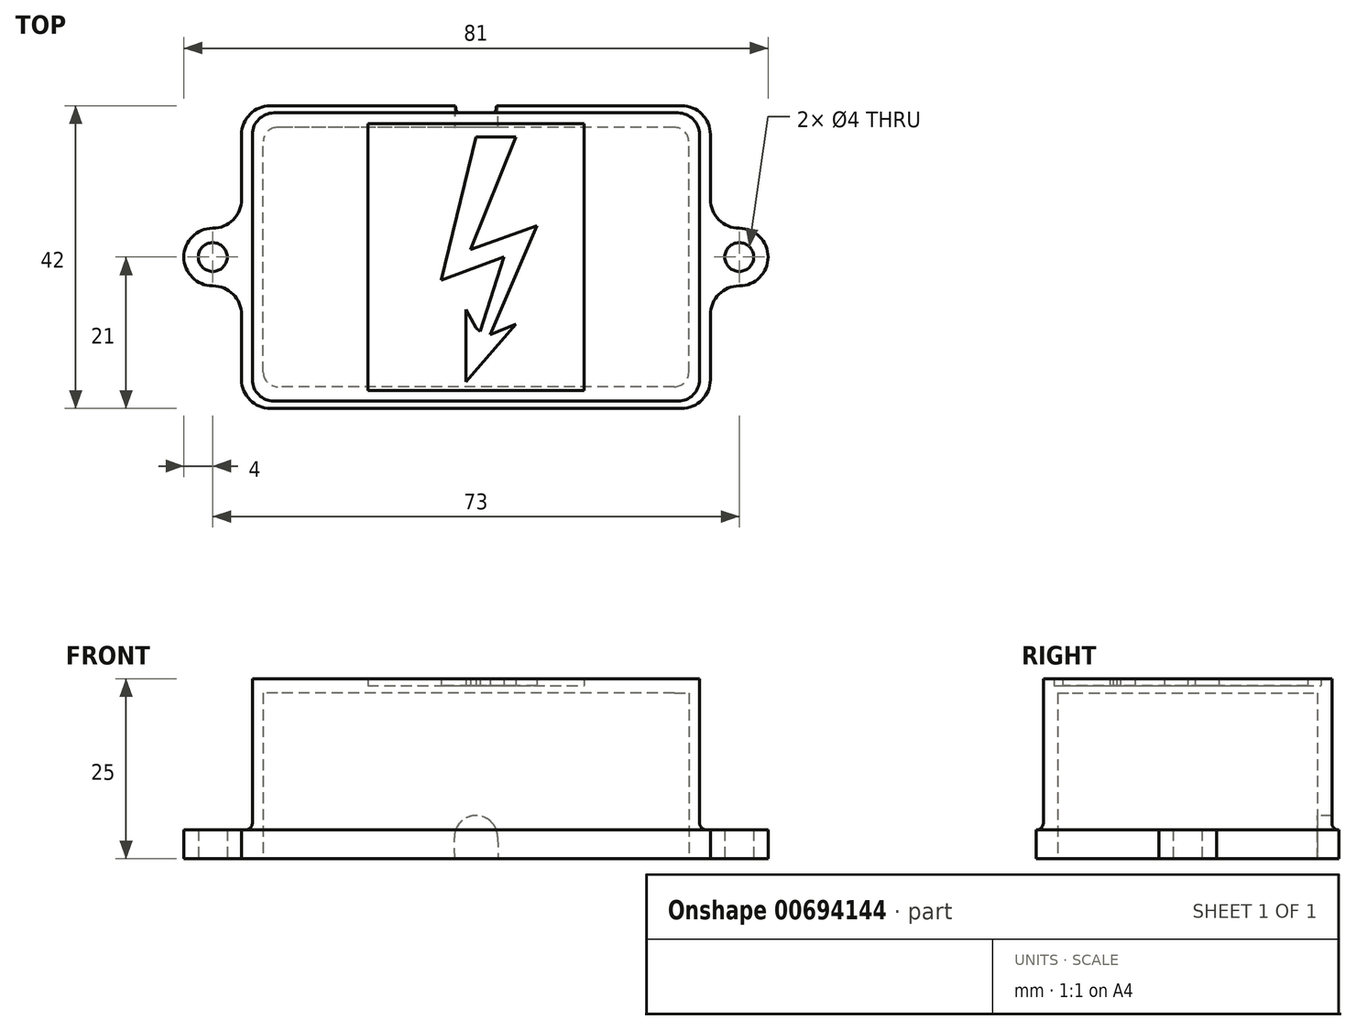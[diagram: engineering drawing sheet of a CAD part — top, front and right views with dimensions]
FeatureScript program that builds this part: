
annotation { "Feature Type Name" : "Feature", "Feature Type Description" : "" }
export const myFeature = defineFeature(function(context is Context, id is Id, definition is map)
    precondition{}
    {
        {
            var Q0;
            Q0=qCreatedBy(makeId("Top.planeOp"),FACE);
            var sketch = newSketch(context, id + "F0", { "sketchPlane" : qUnion([Q0])});
            skLineSegment(sketch, "E0.bottom", {"start": v(-28.5, 21) * mm, "end": v(28.5, 21) * mm});
            skLineSegment(sketch, "E0.top", {"start": v(-28.5, -21) * mm, "end": v(28.5, -21) * mm});
            skLineSegment(sketch, "E0.left", {"start": v(-32.5, 17) * mm, "end": v(-32.5, 8) * mm});
            skLineSegment(sketch, "E0.right", {"start": v(32.5, 17) * mm, "end": v(32.5, 8) * mm});
            skPoint(sketch, "E0.middle", {"position": v(0, 0) * mm});
            skPoint(sketch, "E1.visualSharp", {"position": v(-32.5, 21) * mm});
            skArc(sketch, "E1.filletArc", {"start": v(-28.5, 21) * mm, "mid": v(-31.33, 19.83) * mm, "end": v(-32.5, 17) * mm});
            skPoint(sketch, "E2.visualSharp", {"position": v(-32.5, -21) * mm});
            skArc(sketch, "E2.filletArc", {"start": v(-32.5, -17) * mm, "mid": v(-31.33, -19.83) * mm, "end": v(-28.5, -21) * mm});
            skPoint(sketch, "E3.visualSharp", {"position": v(32.5, -21) * mm});
            skArc(sketch, "E3.filletArc", {"start": v(28.5, -21) * mm, "mid": v(31.33, -19.83) * mm, "end": v(32.5, -17) * mm});
            skPoint(sketch, "E4.visualSharp", {"position": v(32.5, 21) * mm});
            skArc(sketch, "E4.filletArc", {"start": v(32.5, 17) * mm, "mid": v(31.33, 19.83) * mm, "end": v(28.5, 21) * mm});
            skLineSegment(sketch, "E5", {"start": v(0, 0) * mm, "end": v(36.5, 0) * mm, "construction": true});
            skCircle(sketch, "E6", {"center": v(36.5, 0) * mm, "radius": 2 * mm});
            skArc(sketch, "E7", {"start": v(36.5, -4) * mm, "mid": v(40.5, 0) * mm, "end": v(36.5, 4) * mm});
            skLineSegment(sketch, "E8", {"start": v(36.5, -4) * mm, "end": v(36.5, -4) * mm});
            skLineSegment(sketch, "E9.MirrorCS", {"start": v(36.5, 4) * mm, "end": v(36.5, 4) * mm});
            skLineSegment(sketch, "E10.MirrorCS", {"start": v(-36.5, 4) * mm, "end": v(-36.5, 4) * mm});
            skArc(sketch, "E11.MirrorC", {"start": v(-36.5, -4) * mm, "mid": v(-40.5, 0) * mm, "end": v(-36.5, 4) * mm});
            skLineSegment(sketch, "E12.MirrorCS", {"start": v(-36.5, -4) * mm, "end": v(-36.5, -4) * mm});
            skCircle(sketch, "E13.MirrorC", {"center": v(-36.5, 0) * mm, "radius": 2 * mm});
            skLineSegment(sketch, "E14.trimOffspring", {"start": v(-32.5, -8) * mm, "end": v(-32.5, -17) * mm});
            skLineSegment(sketch, "E15.trimOffspring", {"start": v(32.5, -8) * mm, "end": v(32.5, -17) * mm});
            skPoint(sketch, "E16.visualSharp", {"position": v(-32.5, 4) * mm});
            skArc(sketch, "E16.filletArc", {"start": v(-36.5, 4) * mm, "mid": v(-33.67, 5.17) * mm, "end": v(-32.5, 8) * mm});
            skPoint(sketch, "E17.visualSharp", {"position": v(-32.5, -4) * mm});
            skArc(sketch, "E17.filletArc", {"start": v(-32.5, -8) * mm, "mid": v(-33.67, -5.17) * mm, "end": v(-36.5, -4) * mm});
            skPoint(sketch, "E18.visualSharp", {"position": v(32.5, -4) * mm});
            skArc(sketch, "E18.filletArc", {"start": v(36.5, -4) * mm, "mid": v(33.67, -5.17) * mm, "end": v(32.5, -8) * mm});
            skPoint(sketch, "E19.visualSharp", {"position": v(32.5, 4) * mm});
            skArc(sketch, "E19.filletArc", {"start": v(32.5, 8) * mm, "mid": v(33.67, 5.17) * mm, "end": v(36.5, 4) * mm});
            skLineSegment(sketch, "E20.bottom", {"start": v(27.5, -18) * mm, "end": v(-27.5, -18) * mm});
            skLineSegment(sketch, "E20.top", {"start": v(27.5, 18) * mm, "end": v(-27.5, 18) * mm});
            skLineSegment(sketch, "E20.left", {"start": v(29.5, -16) * mm, "end": v(29.5, 16) * mm});
            skLineSegment(sketch, "E20.right", {"start": v(-29.5, -16) * mm, "end": v(-29.5, 16) * mm});
            skPoint(sketch, "E21.visualSharp", {"position": v(-29.5, -18) * mm});
            skArc(sketch, "E21.filletArc", {"start": v(-29.5, -16) * mm, "mid": v(-28.91, -17.41) * mm, "end": v(-27.5, -18) * mm});
            skPoint(sketch, "E22.visualSharp", {"position": v(29.5, 18) * mm});
            skArc(sketch, "E22.filletArc", {"start": v(29.5, 16) * mm, "mid": v(28.91, 17.41) * mm, "end": v(27.5, 18) * mm});
            skPoint(sketch, "E23.visualSharp", {"position": v(29.5, -18) * mm});
            skArc(sketch, "E23.filletArc", {"start": v(27.5, -18) * mm, "mid": v(28.91, -17.41) * mm, "end": v(29.5, -16) * mm});
            skPoint(sketch, "E24.visualSharp", {"position": v(-29.5, 18) * mm});
            skArc(sketch, "E24.filletArc", {"start": v(-27.5, 18) * mm, "mid": v(-28.91, 17.41) * mm, "end": v(-29.5, 16) * mm});
            skSolve(sketch);
        }
        {
            var Q0;
            Q0=makeQuery(id+"F0.imprint","IMPRINT",FACE,{"disambiguationData":[TD([[makeQuery(id+"F0.imprint","IMPRINT",EDGE,{"derivedFrom":sQuery(id+"F0.wireOp",EDGE,"E0.bottom")}),-1.0]])]});
            extrude(context, id + "F1", {"entities" : qUnion([Q0]), "depth" : 4 * mm, "offsetDistance" : 25 * mm});
        }
        {
            var Q0;
            Q0=qCreatedBy(makeId("Top.planeOp"),FACE);
            var sketch = newSketch(context, id + "F2", { "sketchPlane" : qUnion([Q0])});
            skLineSegment(sketch, "E25.bottom", {"start": v(-28, 20) * mm, "end": v(28, 20) * mm});
            skLineSegment(sketch, "E25.top", {"start": v(-28, -20) * mm, "end": v(28, -20) * mm});
            skLineSegment(sketch, "E25.left", {"start": v(-31, 17) * mm, "end": v(-31, -17) * mm});
            skLineSegment(sketch, "E25.right", {"start": v(31, 17) * mm, "end": v(31, -17) * mm});
            skPoint(sketch, "E25.middle", {"position": v(0, 0) * mm});
            skPoint(sketch, "E26.visualSharp", {"position": v(-31, 20) * mm});
            skArc(sketch, "E26.filletArc", {"start": v(-28, 20) * mm, "mid": v(-30.12, 19.12) * mm, "end": v(-31, 17) * mm});
            skPoint(sketch, "E27.visualSharp", {"position": v(31, 20) * mm});
            skArc(sketch, "E27.filletArc", {"start": v(31, 17) * mm, "mid": v(30.12, 19.12) * mm, "end": v(28, 20) * mm});
            skPoint(sketch, "E28.visualSharp", {"position": v(31, -20) * mm});
            skArc(sketch, "E28.filletArc", {"start": v(28, -20) * mm, "mid": v(30.12, -19.12) * mm, "end": v(31, -17) * mm});
            skPoint(sketch, "E29.visualSharp", {"position": v(-31, -20) * mm});
            skArc(sketch, "E29.filletArc", {"start": v(-31, -17) * mm, "mid": v(-30.12, -19.12) * mm, "end": v(-28, -20) * mm});
            skSolve(sketch);
        }
        {
            var Q0;
            Q0 = qSketchRegion(id + "F2", true);
            extrude(context, id + "F3", {"entities" : qUnion([Q0]), "operationType" : NewBodyOperationType.ADD, "depth" : 25 * mm, "offsetDistance" : 25 * mm});
        }
        {
            var Q0;
            Q0=makeQuery(id+"F3.boolean.opBoolean","INTERSECT",EDGE,{"derivedFrom":[makeQuery(id+"F1.opExtrude","CAP_FACE",FACE,{"disambiguationData":[OSD([sQuery(id+"F0.wireOp",EDGE,"E0.bottom"),sQuery(id+"F0.wireOp",EDGE,"E0.top"),sQuery(id+"F0.wireOp",EDGE,"E0.left"),sQuery(id+"F0.wireOp",EDGE,"E0.right"),sQuery(id+"F0.wireOp",EDGE,"E1.filletArc"),sQuery(id+"F0.wireOp",EDGE,"E2.filletArc"),sQuery(id+"F0.wireOp",EDGE,"E3.filletArc"),sQuery(id+"F0.wireOp",EDGE,"E4.filletArc"),sQuery(id+"F0.wireOp",EDGE,"E6"),sQuery(id+"F0.wireOp",EDGE,"E7"),sQuery(id+"F0.wireOp",EDGE,"E11.MirrorC"),sQuery(id+"F0.wireOp",EDGE,"E13.MirrorC"),sQuery(id+"F0.wireOp",EDGE,"E14.trimOffspring"),sQuery(id+"F0.wireOp",EDGE,"E15.trimOffspring"),sQuery(id+"F0.wireOp",EDGE,"E16.filletArc"),sQuery(id+"F0.wireOp",EDGE,"E17.filletArc"),sQuery(id+"F0.wireOp",EDGE,"E18.filletArc"),sQuery(id+"F0.wireOp",EDGE,"E19.filletArc"),sQuery(id+"F0.wireOp",EDGE,"E20.bottom"),sQuery(id+"F0.wireOp",EDGE,"E20.top"),sQuery(id+"F0.wireOp",EDGE,"E20.left"),sQuery(id+"F0.wireOp",EDGE,"E20.right"),sQuery(id+"F0.wireOp",EDGE,"E21.filletArc"),sQuery(id+"F0.wireOp",EDGE,"E22.filletArc"),sQuery(id+"F0.wireOp",EDGE,"E23.filletArc"),sQuery(id+"F0.wireOp",EDGE,"E24.filletArc")])],"isStart":false}),makeQuery(id+"F3.opExtrude","SWEPT_FACE",FACE,{"disambiguationData":[OSD([sQuery(id+"F2.wireOp",EDGE,"E25.top")])]})]});
            var Q1;
            Q1=makeQuery(id+"F3.boolean.opBoolean","INTERSECT",EDGE,{"derivedFrom":[makeQuery(id+"F1.opExtrude","CAP_FACE",FACE,{"disambiguationData":[OSD([sQuery(id+"F0.wireOp",EDGE,"E0.bottom"),sQuery(id+"F0.wireOp",EDGE,"E0.top"),sQuery(id+"F0.wireOp",EDGE,"E0.left"),sQuery(id+"F0.wireOp",EDGE,"E0.right"),sQuery(id+"F0.wireOp",EDGE,"E1.filletArc"),sQuery(id+"F0.wireOp",EDGE,"E2.filletArc"),sQuery(id+"F0.wireOp",EDGE,"E3.filletArc"),sQuery(id+"F0.wireOp",EDGE,"E4.filletArc"),sQuery(id+"F0.wireOp",EDGE,"E6"),sQuery(id+"F0.wireOp",EDGE,"E7"),sQuery(id+"F0.wireOp",EDGE,"E11.MirrorC"),sQuery(id+"F0.wireOp",EDGE,"E13.MirrorC"),sQuery(id+"F0.wireOp",EDGE,"E14.trimOffspring"),sQuery(id+"F0.wireOp",EDGE,"E15.trimOffspring"),sQuery(id+"F0.wireOp",EDGE,"E16.filletArc"),sQuery(id+"F0.wireOp",EDGE,"E17.filletArc"),sQuery(id+"F0.wireOp",EDGE,"E18.filletArc"),sQuery(id+"F0.wireOp",EDGE,"E19.filletArc"),sQuery(id+"F0.wireOp",EDGE,"E20.bottom"),sQuery(id+"F0.wireOp",EDGE,"E20.top"),sQuery(id+"F0.wireOp",EDGE,"E20.left"),sQuery(id+"F0.wireOp",EDGE,"E20.right"),sQuery(id+"F0.wireOp",EDGE,"E21.filletArc"),sQuery(id+"F0.wireOp",EDGE,"E22.filletArc"),sQuery(id+"F0.wireOp",EDGE,"E23.filletArc"),sQuery(id+"F0.wireOp",EDGE,"E24.filletArc")])],"isStart":false}),makeQuery(id+"F3.opExtrude","SWEPT_FACE",FACE,{"disambiguationData":[OSD([sQuery(id+"F2.wireOp",EDGE,"E28.filletArc")])]})]});
            fillet(context, id + "F4", {"entities" : qUnion([Q0, Q1]), "radius" : 1 * mm, "tangentPropagation" : true, "allowEdgeOverflow" : false});
        }
        {
            var Q0;
            Q0=makeQuery(id+"F0.imprint","IMPRINT",FACE,{"disambiguationData":[TD([[makeQuery(id+"F0.imprint","IMPRINT",EDGE,{"derivedFrom":sQuery(id+"F0.wireOp",EDGE,"E20.bottom")}),-1.0]])]});
            extrude(context, id + "F5", {"entities" : qUnion([Q0]), "operationType" : NewBodyOperationType.REMOVE, "depth" : 23 * mm, "offsetDistance" : 25 * mm});
        }
        {
            var Q0;
            Q0=qCreatedBy(makeId("Top.planeOp"),FACE);
            var sketch = newSketch(context, id + "F6", { "sketchPlane" : qUnion([Q0])});
            skLineSegment(sketch, "E30", {"start": v(0, 16.64) * mm, "end": v(5.54, 16.64) * mm});
            skLineSegment(sketch, "E31", {"start": v(5.54, 16.64) * mm, "end": v(-0.76, 1.03) * mm});
            skLineSegment(sketch, "E32", {"start": v(-0.76, 1.03) * mm, "end": v(8.45, 4.35) * mm});
            skLineSegment(sketch, "E33", {"start": v(8.45, 4.35) * mm, "end": v(1.98, -10.77) * mm});
            skLineSegment(sketch, "E34", {"start": v(1.98, -10.77) * mm, "end": v(5.54, -9.32) * mm});
            skLineSegment(sketch, "E35", {"start": v(5.54, -9.32) * mm, "end": v(-1.41, -17.32) * mm});
            skLineSegment(sketch, "E36", {"start": v(-1.41, -17.32) * mm, "end": v(-1.41, -7.3) * mm});
            skLineSegment(sketch, "E37", {"start": v(-1.41, -7.3) * mm, "end": v(0, -9.8) * mm});
            skLineSegment(sketch, "E38", {"start": v(0, -9.8) * mm, "end": v(0.55, -10.34) * mm});
            skLineSegment(sketch, "E39", {"start": v(0.55, -10.34) * mm, "end": v(3.86, 0) * mm});
            skLineSegment(sketch, "E40", {"start": v(3.86, 0) * mm, "end": v(-4.8, -3.22) * mm});
            skLineSegment(sketch, "E41", {"start": v(-4.8, -3.22) * mm, "end": v(0, 16.64) * mm});
            skLineSegment(sketch, "E42.bottom", {"start": v(-15, -18.5) * mm, "end": v(15, -18.5) * mm});
            skLineSegment(sketch, "E42.top", {"start": v(-15, 18.5) * mm, "end": v(15, 18.5) * mm});
            skLineSegment(sketch, "E42.left", {"start": v(-15, -18.5) * mm, "end": v(-15, 18.5) * mm});
            skLineSegment(sketch, "E42.right", {"start": v(15, -18.5) * mm, "end": v(15, 18.5) * mm});
            skPoint(sketch, "E42.middle", {"position": v(0, 0) * mm});
            skSolve(sketch);
        }
        {
            var Q0;
            Q0 = qSketchRegion(id + "F6", true);
            extrude(context, id + "F7", {"entities" : qUnion([Q0]), "operationType" : NewBodyOperationType.REMOVE, "depth" : 30 * mm, "offsetDistance" : 25 * mm, "hasSecondDirection" : true, "secondDirectionOppositeDirection" : false, "secondDirectionDepth" : 24 * mm});
        }
        {
            var Q0;
            Q0=qCreatedBy(makeId("Front.planeOp"),FACE);
            var sketch = newSketch(context, id + "F8", { "sketchPlane" : qUnion([Q0])});
            skLineSegment(sketch, "E43", {"start": v(0, 0) * mm, "end": v(0, 3) * mm, "construction": true});
            skArc(sketch, "E44", {"start": v(3, 3.08) * mm, "mid": v(-0.08, 6) * mm, "end": v(-3, 2.92) * mm});
            skLineSegment(sketch, "E45", {"start": v(-3, 2.92) * mm, "end": v(-2.8, -4.51) * mm});
            skLineSegment(sketch, "E46", {"start": v(-2.8, -4.51) * mm, "end": v(3.2, -4.51) * mm});
            skLineSegment(sketch, "E47", {"start": v(3.2, -4.51) * mm, "end": v(3, 3.08) * mm});
            skSolve(sketch);
        }
        {
            var Q0;
            Q0=makeQuery(id+"F8.imprint","IMPRINT",FACE,{"disambiguationData":[TD([[makeQuery(id+"F8.imprint","IMPRINT",EDGE,{"derivedFrom":sQuery(id+"F8.wireOp",EDGE,"E44")}),1.0]])]});
            extrude(context, id + "F9", {"entities" : qUnion([Q0]), "operationType" : NewBodyOperationType.REMOVE, "oppositeDirection" : true, "depth" : 25 * mm, "offsetDistance" : 25 * mm});
        }
    });
